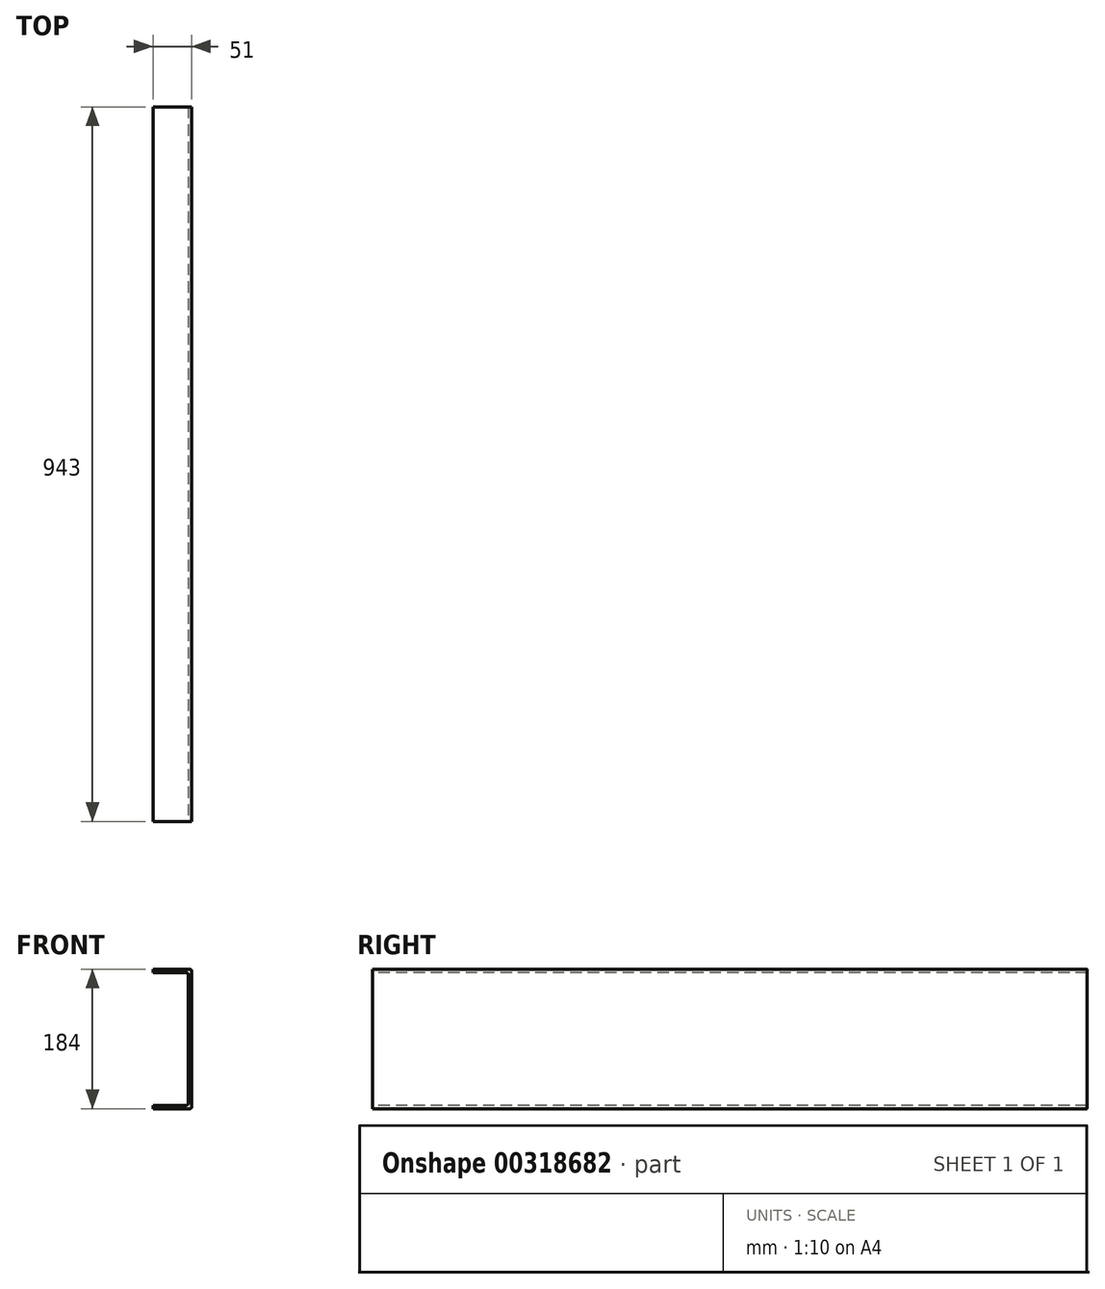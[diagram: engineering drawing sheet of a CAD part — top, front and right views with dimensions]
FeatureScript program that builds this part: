
annotation { "Feature Type Name" : "Feature", "Feature Type Description" : "" }
export const myFeature = defineFeature(function(context is Context, id is Id, definition is map)
    precondition{}
    {
        {
            var Q0;
            Q0=qCreatedBy(makeId("Right.planeOp"),FACE);
            var sketch = newSketch(context, id + "F0", { "sketchPlane" : qUnion([Q0])});
            skLineSegment(sketch, "E0.bottom", {"start": v(471.5, -92) * mm, "end": v(-471.5, -92) * mm});
            skLineSegment(sketch, "E0.top", {"start": v(471.5, 92) * mm, "end": v(-471.5, 92) * mm});
            skLineSegment(sketch, "E0.left", {"start": v(471.5, -92) * mm, "end": v(471.5, 92) * mm});
            skLineSegment(sketch, "E0.right", {"start": v(-471.5, -92) * mm, "end": v(-471.5, 92) * mm});
            skPoint(sketch, "E0.middle", {"position": v(0, 0) * mm});
            skSolve(sketch);
        }
        {
            var Q0;
            Q0=sQuery(id+"F0.wireOp",EDGE,"E0.bottom");
            var Q1;
            Q1=sQuery(id+"F0.wireOp",VERTEX,"E0.right.end");
            cPlane(context, id + "F1", {"entities" : qUnion([Q0, Q1]), "cplaneType" : CPlaneType.LINE_POINT, "offset" : 25 * mm, "width" : 150 * mm, "height" : 150 * mm});
        }
        {
            var Q0;
            Q0=qCreatedBy(id+"F1.planeOp",FACE);
            var sketch = newSketch(context, id + "F2", { "sketchPlane" : qUnion([Q0])});
            skLineSegment(sketch, "E1.0", {"start": v(0, -89.5) * mm, "end": v(0, 89.5) * mm});
            skLineSegment(sketch, "E2", {"start": v(-2.5, 92) * mm, "end": v(-51, 92) * mm});
            skLineSegment(sketch, "E3", {"start": v(-2.5, -92) * mm, "end": v(-51, -92) * mm});
            skLineSegment(sketch, "E4.0", {"start": v(-7, 87.5) * mm, "end": v(-51, 87.5) * mm});
            skLineSegment(sketch, "E4.1", {"start": v(-4.5, -85) * mm, "end": v(-4.5, 85) * mm});
            skLineSegment(sketch, "E4.2", {"start": v(-7, -87.5) * mm, "end": v(-51, -87.5) * mm});
            skLineSegment(sketch, "E5", {"start": v(-51, 92) * mm, "end": v(-51, 87.5) * mm});
            skLineSegment(sketch, "E6", {"start": v(-51, -87.5) * mm, "end": v(-51, -92) * mm});
            skPoint(sketch, "E7.visualSharp", {"position": v(-4.5, 87.5) * mm});
            skArc(sketch, "E7.filletArc", {"start": v(-4.5, 85) * mm, "mid": v(-5.23, 86.77) * mm, "end": v(-7, 87.5) * mm});
            skPoint(sketch, "E8.visualSharp", {"position": v(0, 92) * mm});
            skArc(sketch, "E8.filletArc", {"start": v(0, 89.5) * mm, "mid": v(-0.73, 91.27) * mm, "end": v(-2.5, 92) * mm});
            skPoint(sketch, "E9.visualSharp", {"position": v(-4.5, -87.5) * mm});
            skArc(sketch, "E9.filletArc", {"start": v(-7, -87.5) * mm, "mid": v(-5.23, -86.77) * mm, "end": v(-4.5, -85) * mm});
            skPoint(sketch, "E10.visualSharp", {"position": v(0, -92) * mm});
            skArc(sketch, "E10.filletArc", {"start": v(-2.5, -92) * mm, "mid": v(-0.73, -91.27) * mm, "end": v(0, -89.5) * mm});
            skSolve(sketch);
        }
        {
            var Q0;
            Q0=makeQuery(id+"F2.imprint","IMPRINT",FACE,{"disambiguationData":[TD([[makeQuery(id+"F2.imprint","IMPRINT",EDGE,{"derivedFrom":sQuery(id+"F2.wireOp",EDGE,"E1.0")}),1.0]])]});
            var Q1;
            Q1=sQuery(id+"F0.wireOp",VERTEX,"E0.left.end");
            extrude(context, id + "F3", {"entities" : qUnion([Q0]), "endBound" : BoundingType.UP_TO_VERTEX, "oppositeDirection" : true, "endBoundEntityVertex" : qUnion([Q1]), "depth" : 25 * mm});
        }
    });
